# Revit family: Sky Lighting AS - Sky Pullert_upd
name_source: partatom
category: Lighting Fixtures
revit_build: Autodesk Revit 2014 (Build: 20130308_1515(x64)
units: mm (PartAtom-declared; Revit-internal decimal feet)

## types (4) — shared parameters
BIMobject category = Lighting
CRI = 90
Color Filter = 65535
Conv.factor = 1
Date of publishing = 2015-10-28
Depth = 186 mm
Design country = Denmark
Dimming Lamp Color Temperature Shift = <None>
Edition number = 1
Height = 1042 mm  [stored 3.41864 ft]
IFC Classification = Light Fixture
Installation instructions = http://www.focus-lighting.dk
Light Output Ratio Downwards = 50,5%
Light Output Ratio Total = 56,7%
Light Source Symbol Size = 400 mm
Lightsources = 1
Manufacturer country = Denmark
Manufacturer name = Focus Lighting
Product Guid = 5406db22-cfeb-4111-bcb8-bec333450793
Product SKU = 7830-9930
Product data url = https://bimobject.com
Product family = Outdoor
Product group = Bollards
QR code = http://bimobject.com
Technical description = http://www.focus-lighting.dk
Tilt-angle = 0°
UNSPSC Code = 3911
Weight Net (Kg) = 10
Width = 186 mm
Youtube clip = https://www.youtube.com
zero-valued in all types: Nominal height, Nominal width

## per-type parameters (varying)
| type | Date / name | Luminaire | Test Report | Type | Wattage Comments |
| Sky Pullert_9W_270.ldt | 17-09-2015/DC/Focus Lighting AS | Sky Pullert_9W_927 | 20150917.1 | V8_27G0800-2x_350mA | 9 W
9 W |
| Sky Pullert_9W_930.ldt | 17-09-2015/DC/Focus Lighting AS | Sky Pullert_9W_930 | 20150917.2 | V8_30G0800-2x_350mA | 9 W
9 W |
| Sky Pullert_12W_927.ldt | 16-09-2015/DC/Focus Lighting AS | Sky Pullert_12W_927 | 20150916.1 | V8_27G0800-2x_500mA | 12 W
9 W |
| Sky Pullert_12W_930.ldt | 15-09-2015/DC/Focus Lighting AS | Sky Pullert_12W_930 | 20150915.3 | V8_30G0800-2x_500mA | 12 W
9 W |

note: column(s) folded — value = type name in every type: Lamp

note: [stored X ft] marks values corroborated as IEEE doubles in the binary element streams (Revit-internal decimal feet)

## geometry (parser evidence)
native form markers: Sweep x6
no freeform markers — native parametric forms only
